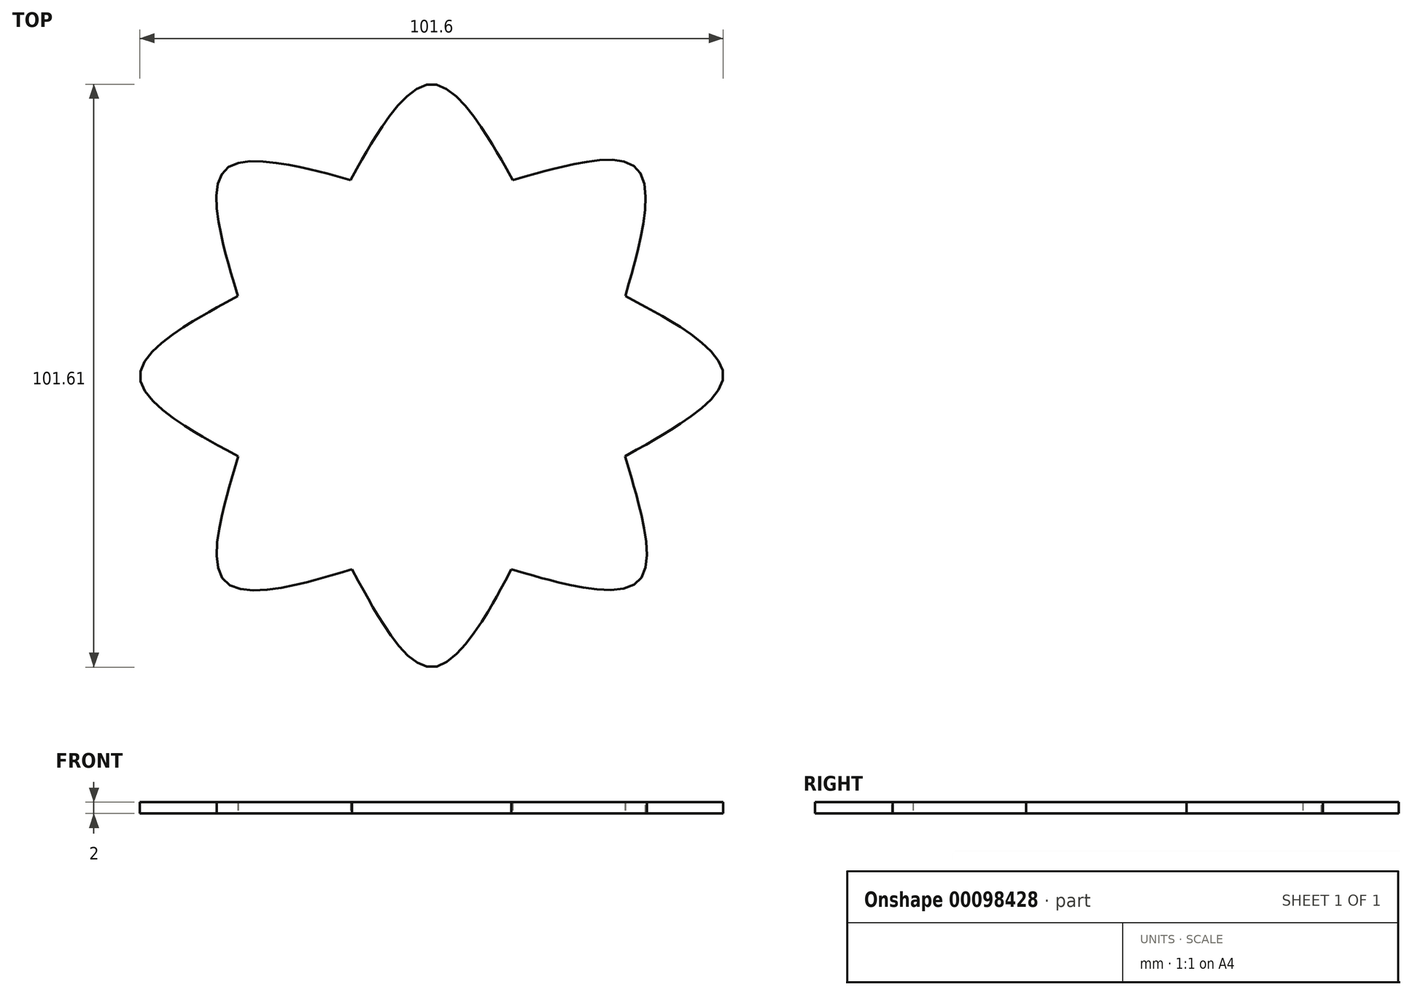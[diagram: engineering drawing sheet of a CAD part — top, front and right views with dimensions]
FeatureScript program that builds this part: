
annotation { "Feature Type Name" : "Feature", "Feature Type Description" : "" }
export const myFeature = defineFeature(function(context is Context, id is Id, definition is map)
    precondition{}
    {
        {
            var Q0;
            Q0=qCreatedBy(makeId("Top.planeOp"),FACE);
            var sketch = newSketch(context, id + "F0", { "sketchPlane" : qUnion([Q0])});
            skPoint(sketch, "E0.center", {"position": v(0, 0) * mm});
            skFitSpline(sketch, "E1", {"points": [v(-14.13, 34.1) * mm, v(-9.3, 42.32) * mm, v(0, 50.8) * mm, v(9.38, 42.2) * mm, v(14.13, 34.1) * mm], "startDerivative": vector(28.25, 50.1) * mm, "endDerivative": vector(28.25, -50.1) * mm});
            skFitSpline(sketch, "E2", {"points": [v(14.13, 34.1) * mm, v(23.75, 36.64) * mm, v(35.83, 36.02) * mm, v(36.06, 22.44) * mm, v(33.74, 13.87) * mm], "startDerivative": vector(55.51, 15.76) * mm, "endDerivative": vector(-16.17, -56.1) * mm});
            skFitSpline(sketch, "E3", {"points": [v(33.74, 13.87) * mm, v(42.22, 9.14) * mm, v(50.8, 0.13) * mm, v(42.54, -8.9) * mm, v(33.66, -14.05) * mm], "startDerivative": vector(51.3, -27.42) * mm, "endDerivative": vector(-51.3, -28.42) * mm});
            skFitSpline(sketch, "E4", {"points": [v(33.66, -14.05) * mm, v(36.15, -22.7) * mm, v(36.02, -35.83) * mm, v(22.27, -36.05) * mm, v(13.87, -33.74) * mm], "startDerivative": vector(16.88, -55.66) * mm, "endDerivative": vector(-56.37, 16.19) * mm});
            skFitSpline(sketch, "E5", {"points": [v(13.87, -33.74) * mm, v(9.71, -41.27) * mm, v(0.13, -50.8) * mm, v(-8.78, -42.7) * mm, v(-13.87, -33.74) * mm], "startDerivative": vector(-27.42, -51.23) * mm, "endDerivative": vector(-28.07, 51.16) * mm});
            skFitSpline(sketch, "E6", {"points": [v(-13.87, -33.74) * mm, v(-21.7, -35.97) * mm, v(-35.83, -36.02) * mm, v(-36.23, -23.13) * mm, v(-33.66, -14.05) * mm], "startDerivative": vector(-55.97, -16.68) * mm, "endDerivative": vector(16.38, 56.06) * mm});
            skFitSpline(sketch, "E7", {"points": [v(-33.66, -14.05) * mm, v(-41.7, -9.54) * mm, v(-50.8, -0.13) * mm, v(-42.13, 9.1) * mm, v(-33.74, 13.87) * mm], "startDerivative": vector(-51.37, 27.78) * mm, "endDerivative": vector(51.23, 28.06) * mm});
            skFitSpline(sketch, "E8", {"points": [v(-33.74, 13.87) * mm, v(-36.47, 23.7) * mm, v(-36.02, 35.83) * mm, v(-23.74, 36.5) * mm, v(-14.13, 34.1) * mm], "startDerivative": vector(-16.67, 55.7) * mm, "endDerivative": vector(55.92, -15.26) * mm});
            skLineSegment(sketch, "E9", {"start": v(-50.8, -0.13) * mm, "end": v(50.8, 0.13) * mm, "construction": true});
            skSolve(sketch);
        }
        {
            var Q0;
            Q0=makeQuery(id+"F0.imprint","IMPRINT",FACE,{"disambiguationData":[TD([[makeQuery(id+"F0.imprint","IMPRINT",EDGE,{"derivedFrom":sQuery(id+"F0.wireOp",EDGE,"E1")}),-1.0]])]});
            extrude(context, id + "F1", {"entities" : qUnion([Q0]), "depth" : 2 * mm});
        }
        {
            var Q0;
            Q0=makeQuery(id+"F1.opExtrude","SWEPT_BODY",BODY,{"disambiguationData":[OSD([sQuery(id+"F0.wireOp",EDGE,"E1"),sQuery(id+"F0.wireOp",EDGE,"E2"),sQuery(id+"F0.wireOp",EDGE,"E3"),sQuery(id+"F0.wireOp",EDGE,"E4"),sQuery(id+"F0.wireOp",EDGE,"E5"),sQuery(id+"F0.wireOp",EDGE,"E6"),sQuery(id+"F0.wireOp",EDGE,"E7"),sQuery(id+"F0.wireOp",EDGE,"E8")])]});
            transform(context, id + "F2", {"entities" : qUnion([Q0]), "transformType" : TransformType.TRANSLATION_3D, "dx" : 0 * mm, "dy" : 0 * mm, "dz" : 0 * mm, "makeCopy" : true});
        }
    });
